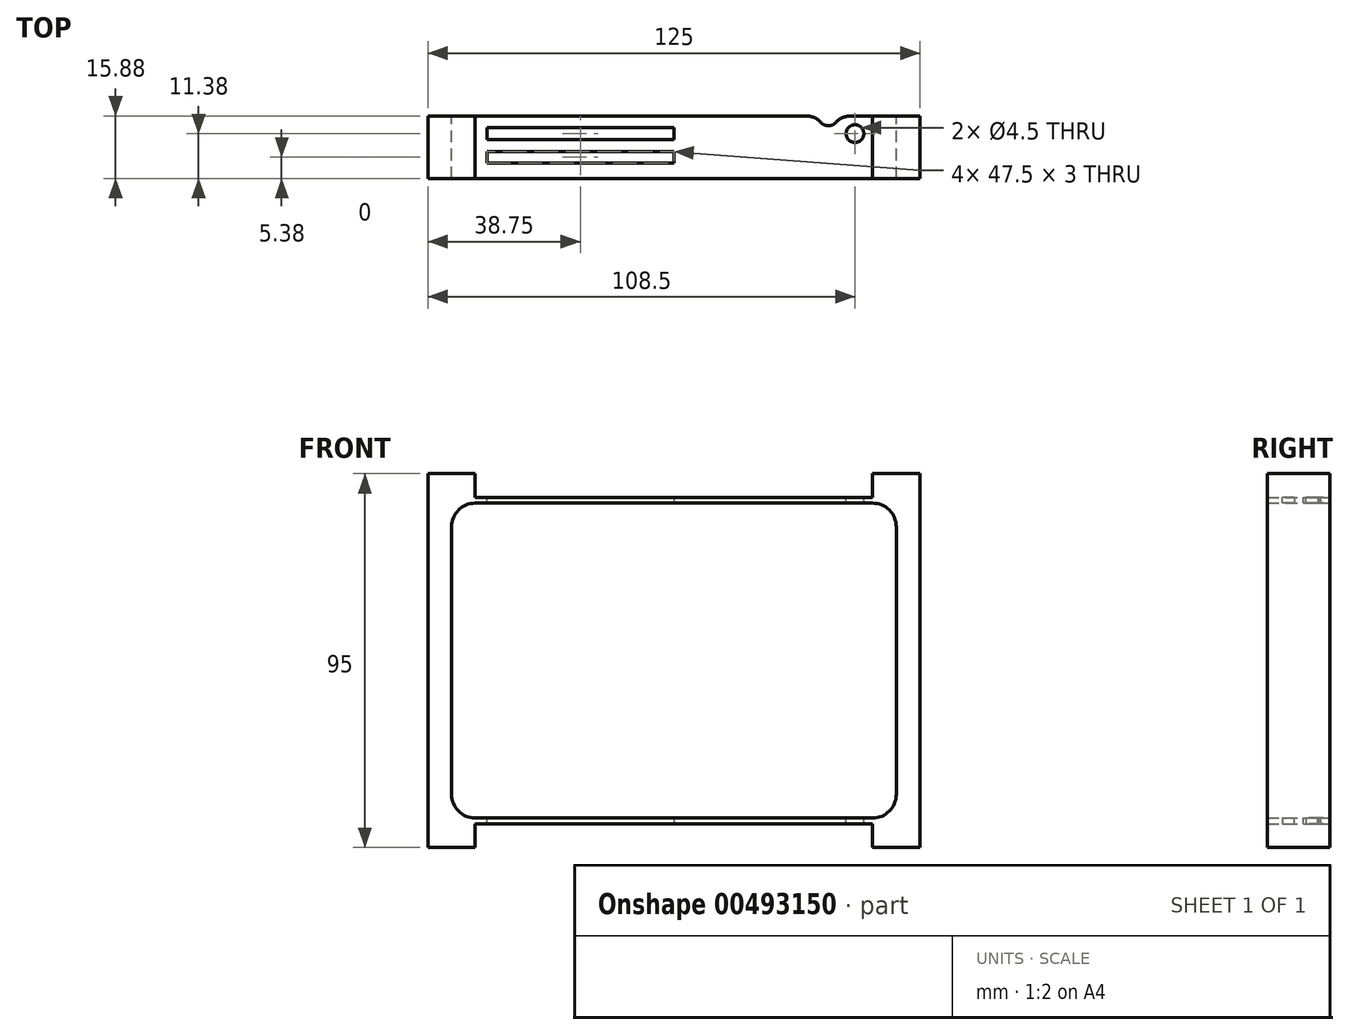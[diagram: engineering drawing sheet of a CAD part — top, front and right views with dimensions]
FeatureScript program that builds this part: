
annotation { "Feature Type Name" : "Feature", "Feature Type Description" : "" }
export const myFeature = defineFeature(function(context is Context, id is Id, definition is map)
    precondition{}
    {
        {
            var Q0;
            Q0=qCreatedBy(makeId("Front.planeOp"),FACE);
            var sketch = newSketch(context, id + "F0", { "sketchPlane" : qUnion([Q0])});
            skLineSegment(sketch, "E0.bottom", {"start": v(62.5, 47.5) * mm, "end": v(-62.5, 47.5) * mm, "construction": true});
            skLineSegment(sketch, "E0.top", {"start": v(62.5, -47.5) * mm, "end": v(-62.5, -47.5) * mm, "construction": true});
            skLineSegment(sketch, "E0.left", {"start": v(62.5, 47.5) * mm, "end": v(62.5, -47.5) * mm, "construction": true});
            skLineSegment(sketch, "E0.right", {"start": v(-62.5, 47.5) * mm, "end": v(-62.5, -47.5) * mm, "construction": true});
            skPoint(sketch, "E0.middle", {"position": v(0, 0) * mm});
            skLineSegment(sketch, "E1", {"start": v(-62.5, 47.5) * mm, "end": v(-50.5, 47.5) * mm});
            skLineSegment(sketch, "E2", {"start": v(62.5, 47.5) * mm, "end": v(50.5, 47.5) * mm});
            skLineSegment(sketch, "E3", {"start": v(50.5, 47.5) * mm, "end": v(50.5, 41.5) * mm});
            skLineSegment(sketch, "E4", {"start": v(50.5, 41.5) * mm, "end": v(-50.5, 41.5) * mm});
            skLineSegment(sketch, "E5", {"start": v(-50.5, 41.5) * mm, "end": v(-50.5, 47.5) * mm});
            skLineSegment(sketch, "E6", {"start": v(62.5, 47.5) * mm, "end": v(62.5, -47.5) * mm});
            skLineSegment(sketch, "E7", {"start": v(-62.5, -47.5) * mm, "end": v(-62.5, 47.5) * mm});
            skLineSegment(sketch, "E8", {"start": v(62.5, -47.5) * mm, "end": v(50.5, -47.5) * mm});
            skLineSegment(sketch, "E9", {"start": v(50.5, -47.5) * mm, "end": v(50.5, -41.5) * mm});
            skLineSegment(sketch, "E10", {"start": v(50.5, -41.5) * mm, "end": v(-50.5, -41.5) * mm});
            skLineSegment(sketch, "E11", {"start": v(-50.5, -41.5) * mm, "end": v(-50.5, -47.5) * mm});
            skLineSegment(sketch, "E12", {"start": v(-50.5, -47.5) * mm, "end": v(-62.5, -47.5) * mm});
            skLineSegment(sketch, "E13.bottom", {"start": v(56.5, 40) * mm, "end": v(-56.5, 40) * mm, "construction": true});
            skLineSegment(sketch, "E13.top", {"start": v(56.5, -40) * mm, "end": v(-56.5, -40) * mm, "construction": true});
            skLineSegment(sketch, "E13.left", {"start": v(56.5, 40) * mm, "end": v(56.5, -40) * mm, "construction": true});
            skLineSegment(sketch, "E13.right", {"start": v(-56.5, 40) * mm, "end": v(-56.5, -40) * mm, "construction": true});
            skLineSegment(sketch, "E14.bottom", {"start": v(56.5, 40) * mm, "end": v(-56.5, 40) * mm});
            skLineSegment(sketch, "E14.top", {"start": v(56.5, -40) * mm, "end": v(-56.5, -40) * mm});
            skLineSegment(sketch, "E14.left", {"start": v(56.5, 40) * mm, "end": v(56.5, -40) * mm});
            skLineSegment(sketch, "E14.right", {"start": v(-56.5, 40) * mm, "end": v(-56.5, -40) * mm});
            skSolve(sketch);
        }
        {
            var Q0;
            Q0=qSketchRegion(id+"F0",true);
            extrude(context, id + "F1", {"entities" : qUnion([Q0]), "depth" : 15.88 * mm});
        }
        {
            var Q0;
            Q0=makeQuery(id+"F1.opExtrude","SWEPT_EDGE",EDGE,{"disambiguationData":[OSD([sQuery(id+"F0.wireOp",EDGE,"E14.bottom"),sQuery(id+"F0.wireOp",EDGE,"E14.left")])]});
            var Q1;
            Q1=makeQuery(id+"F1.opExtrude","SWEPT_EDGE",EDGE,{"disambiguationData":[OSD([sQuery(id+"F0.wireOp",EDGE,"E14.top"),sQuery(id+"F0.wireOp",EDGE,"E14.left")])]});
            var Q2;
            Q2=makeQuery(id+"F1.opExtrude","SWEPT_EDGE",EDGE,{"disambiguationData":[OSD([sQuery(id+"F0.wireOp",EDGE,"E14.top"),sQuery(id+"F0.wireOp",EDGE,"E14.right")])]});
            var Q3;
            Q3=makeQuery(id+"F1.opExtrude","SWEPT_EDGE",EDGE,{"disambiguationData":[OSD([sQuery(id+"F0.wireOp",EDGE,"E14.bottom"),sQuery(id+"F0.wireOp",EDGE,"E14.right")])]});
            fillet(context, id + "F2", {"entities" : qUnion([Q0, Q1, Q2, Q3]), "radius" : 6 * mm, "tangentPropagation" : true, "allowEdgeOverflow" : false});
        }
        {
            var Q0;
            Q0=makeQuery(id+"F1.opExtrude","SWEPT_FACE",FACE,{"disambiguationData":[OSD([sQuery(id+"F0.wireOp",EDGE,"E4")])]});
            var sketch = newSketch(context, id + "F3", { "sketchPlane" : qUnion([Q0])});
            skLineSegment(sketch, "E15.bottom", {"start": v(-47.5, -3) * mm, "end": v(41.5, -3) * mm});
            skLineSegment(sketch, "E15.top", {"start": v(-47.5, -6) * mm, "end": v(41.5, -6) * mm});
            skLineSegment(sketch, "E15.left", {"start": v(-47.5, -3) * mm, "end": v(-47.5, -6) * mm});
            skLineSegment(sketch, "E15.right", {"start": v(41.5, -3) * mm, "end": v(41.5, -6) * mm});
            skLineSegment(sketch, "E16.bottom", {"start": v(-47.5, -9) * mm, "end": v(47.5, -9) * mm});
            skLineSegment(sketch, "E16.top", {"start": v(-47.5, -12) * mm, "end": v(47.5, -12) * mm});
            skLineSegment(sketch, "E16.left", {"start": v(-47.5, -9) * mm, "end": v(-47.5, -12) * mm});
            skLineSegment(sketch, "E16.right", {"start": v(47.5, -9) * mm, "end": v(47.5, -12) * mm});
            skCircle(sketch, "E17", {"center": v(46, -4.5) * mm, "radius": 1.5 * mm});
            skSolve(sketch);
        }
        {
            var Q0;
            Q0=qSketchRegion(id+"F3",true);
            extrude(context, id + "F4", {"entities" : qUnion([Q0]), "operationType" : NewBodyOperationType.REMOVE, "oppositeDirection" : true, "depth" : 132 * mm});
        }
        {
            var Q0;
            Q0=makeQuery(id+"F1.opExtrude","SWEPT_FACE",FACE,{"disambiguationData":[OSD([sQuery(id+"F0.wireOp",EDGE,"E4")])]});
            var sketch = newSketch(context, id + "F5", { "sketchPlane" : qUnion([Q0])});
            skLineSegment(sketch, "E18.bottom", {"start": v(0, 0) * mm, "end": v(42.94, 0) * mm});
            skLineSegment(sketch, "E18.top", {"start": v(0, -7.4) * mm, "end": v(42.94, -7.4) * mm});
            skLineSegment(sketch, "E18.left", {"start": v(0, 0) * mm, "end": v(0, -7.4) * mm});
            skLineSegment(sketch, "E18.right", {"start": v(42.94, 0) * mm, "end": v(42.94, -7.4) * mm});
            skLineSegment(sketch, "E19.bottom", {"start": v(0, -7.4) * mm, "end": v(49.14, -7.4) * mm});
            skLineSegment(sketch, "E19.top", {"start": v(0, -14.14) * mm, "end": v(49.14, -14.14) * mm});
            skLineSegment(sketch, "E19.left", {"start": v(0, -7.4) * mm, "end": v(0, -14.14) * mm});
            skLineSegment(sketch, "E19.right", {"start": v(49.14, -7.4) * mm, "end": v(49.14, -14.14) * mm});
            skSolve(sketch);
        }
        {
            var Q0;
            Q0=qSketchRegion(id+"F5",true);
            extrude(context, id + "F6", {"entities" : qUnion([Q0]), "operationType" : NewBodyOperationType.ADD, "oppositeDirection" : true, "depth" : 1.5 * mm});
        }
        {
            var Q0;
            Q0=makeQuery(id+"F1.opExtrude","SWEPT_FACE",FACE,{"disambiguationData":[OSD([sQuery(id+"F0.wireOp",EDGE,"E10")])]});
            var sketch = newSketch(context, id + "F7", { "sketchPlane" : qUnion([Q0])});
            skLineSegment(sketch, "E20.bottom", {"start": v(0, 15.88) * mm, "end": v(49.01, 15.88) * mm});
            skLineSegment(sketch, "E20.top", {"start": v(0, 7.24) * mm, "end": v(49.01, 7.24) * mm});
            skLineSegment(sketch, "E20.left", {"start": v(0, 15.88) * mm, "end": v(0, 7.24) * mm});
            skLineSegment(sketch, "E20.right", {"start": v(49.01, 15.88) * mm, "end": v(49.01, 7.24) * mm});
            skLineSegment(sketch, "E21.bottom", {"start": v(0, 0) * mm, "end": v(42.8, 0) * mm});
            skLineSegment(sketch, "E21.top", {"start": v(0, 7.24) * mm, "end": v(42.8, 7.24) * mm});
            skLineSegment(sketch, "E21.left", {"start": v(0, 0) * mm, "end": v(0, 7.24) * mm});
            skLineSegment(sketch, "E21.right", {"start": v(42.8, 0) * mm, "end": v(42.8, 7.24) * mm});
            skSolve(sketch);
        }
        {
            var Q0;
            Q0=qSketchRegion(id+"F7",true);
            extrude(context, id + "F8", {"entities" : qUnion([Q0]), "operationType" : NewBodyOperationType.ADD, "oppositeDirection" : true, "depth" : 1.5 * mm});
        }
        {
            var Q0;
            Q0=makeQuery(id+"F6.boolean.opBoolean","MERGE",FACE,{"derivedFrom":[makeQuery(id+"F1.opExtrude","SWEPT_FACE",FACE,{"disambiguationData":[OSD([sQuery(id+"F0.wireOp",EDGE,"E4")])]}),makeQuery(id+"F6.opExtrude","CAP_FACE",FACE,{"disambiguationData":[OSD([sQuery(id+"F5.wireOp",EDGE,"E18.bottom"),sQuery(id+"F5.wireOp",EDGE,"E18.left"),sQuery(id+"F5.wireOp",EDGE,"E18.right"),sQuery(id+"F5.wireOp",EDGE,"E19.bottom"),sQuery(id+"F5.wireOp",EDGE,"E19.top"),sQuery(id+"F5.wireOp",EDGE,"E19.left"),sQuery(id+"F5.wireOp",EDGE,"E19.right")])],"isStart":true})]});
            var sketch = newSketch(context, id + "F9", { "sketchPlane" : qUnion([Q0])});
            skCircle(sketch, "E22", {"center": v(39.25, 0) * mm, "radius": 2.5 * mm});
            skSolve(sketch);
        }
        {
            var Q0;
            Q0=qSketchRegion(id+"F9",true);
            extrude(context, id + "F10", {"entities" : qUnion([Q0]), "operationType" : NewBodyOperationType.REMOVE, "oppositeDirection" : true, "depth" : 92 * mm});
        }
        {
            var Q0;
            Q0=makeQuery(id+"F6.boolean.opBoolean","MERGE",FACE,{"derivedFrom":[makeQuery(id+"F1.opExtrude","SWEPT_FACE",FACE,{"disambiguationData":[OSD([sQuery(id+"F0.wireOp",EDGE,"E4")])]}),makeQuery(id+"F6.opExtrude","CAP_FACE",FACE,{"disambiguationData":[OSD([sQuery(id+"F5.wireOp",EDGE,"E18.bottom"),sQuery(id+"F5.wireOp",EDGE,"E18.left"),sQuery(id+"F5.wireOp",EDGE,"E18.right"),sQuery(id+"F5.wireOp",EDGE,"E19.bottom"),sQuery(id+"F5.wireOp",EDGE,"E19.top"),sQuery(id+"F5.wireOp",EDGE,"E19.left"),sQuery(id+"F5.wireOp",EDGE,"E19.right")])],"isStart":true})]});
            var sketch = newSketch(context, id + "F11", { "sketchPlane" : qUnion([Q0])});
            skCircle(sketch, "E23", {"center": v(46, -4.5) * mm, "radius": 2.25 * mm});
            skSolve(sketch);
        }
        {
            var Q0;
            Q0=qSketchRegion(id+"F11",true);
            extrude(context, id + "F12", {"entities" : qUnion([Q0]), "operationType" : NewBodyOperationType.REMOVE, "oppositeDirection" : true, "depth" : 200 * mm});
        }
        {
            var Q0;
            Q0=makeQuery(id+"F10.boolean.opBoolean","INTERSECT",EDGE,{"disambiguationData":[OD(2.0)],"derivedFrom":[makeQuery(id+"F1.opExtrude","CAP_FACE",FACE,{"disambiguationData":[OSD([sQuery(id+"F0.wireOp",EDGE,"E1"),sQuery(id+"F0.wireOp",EDGE,"E2"),sQuery(id+"F0.wireOp",EDGE,"E3"),sQuery(id+"F0.wireOp",EDGE,"E4"),sQuery(id+"F0.wireOp",EDGE,"E5"),sQuery(id+"F0.wireOp",EDGE,"E6"),sQuery(id+"F0.wireOp",EDGE,"E7"),sQuery(id+"F0.wireOp",EDGE,"E8"),sQuery(id+"F0.wireOp",EDGE,"E9"),sQuery(id+"F0.wireOp",EDGE,"E10"),sQuery(id+"F0.wireOp",EDGE,"E11"),sQuery(id+"F0.wireOp",EDGE,"E12"),sQuery(id+"F0.wireOp",EDGE,"E14.bottom"),sQuery(id+"F0.wireOp",EDGE,"E14.top"),sQuery(id+"F0.wireOp",EDGE,"E14.left"),sQuery(id+"F0.wireOp",EDGE,"E14.right")])],"isStart":true}),makeQuery(id+"F10.opExtrude","SWEPT_FACE",FACE,{"disambiguationData":[OSD([sQuery(id+"F9.wireOp",EDGE,"E22")])]})]});
            var Q1;
            Q1=makeQuery(id+"F10.boolean.opBoolean","INTERSECT",EDGE,{"disambiguationData":[OD(3.0)],"derivedFrom":[makeQuery(id+"F1.opExtrude","CAP_FACE",FACE,{"disambiguationData":[OSD([sQuery(id+"F0.wireOp",EDGE,"E1"),sQuery(id+"F0.wireOp",EDGE,"E2"),sQuery(id+"F0.wireOp",EDGE,"E3"),sQuery(id+"F0.wireOp",EDGE,"E4"),sQuery(id+"F0.wireOp",EDGE,"E5"),sQuery(id+"F0.wireOp",EDGE,"E6"),sQuery(id+"F0.wireOp",EDGE,"E7"),sQuery(id+"F0.wireOp",EDGE,"E8"),sQuery(id+"F0.wireOp",EDGE,"E9"),sQuery(id+"F0.wireOp",EDGE,"E10"),sQuery(id+"F0.wireOp",EDGE,"E11"),sQuery(id+"F0.wireOp",EDGE,"E12"),sQuery(id+"F0.wireOp",EDGE,"E14.bottom"),sQuery(id+"F0.wireOp",EDGE,"E14.top"),sQuery(id+"F0.wireOp",EDGE,"E14.left"),sQuery(id+"F0.wireOp",EDGE,"E14.right")])],"isStart":true}),makeQuery(id+"F10.opExtrude","SWEPT_FACE",FACE,{"disambiguationData":[OSD([sQuery(id+"F9.wireOp",EDGE,"E22")])]})]});
            fillet(context, id + "F13", {"entities" : qUnion([Q0, Q1]), "radius" : 5 * mm, "tangentPropagation" : true, "allowEdgeOverflow" : false});
        }
    });
